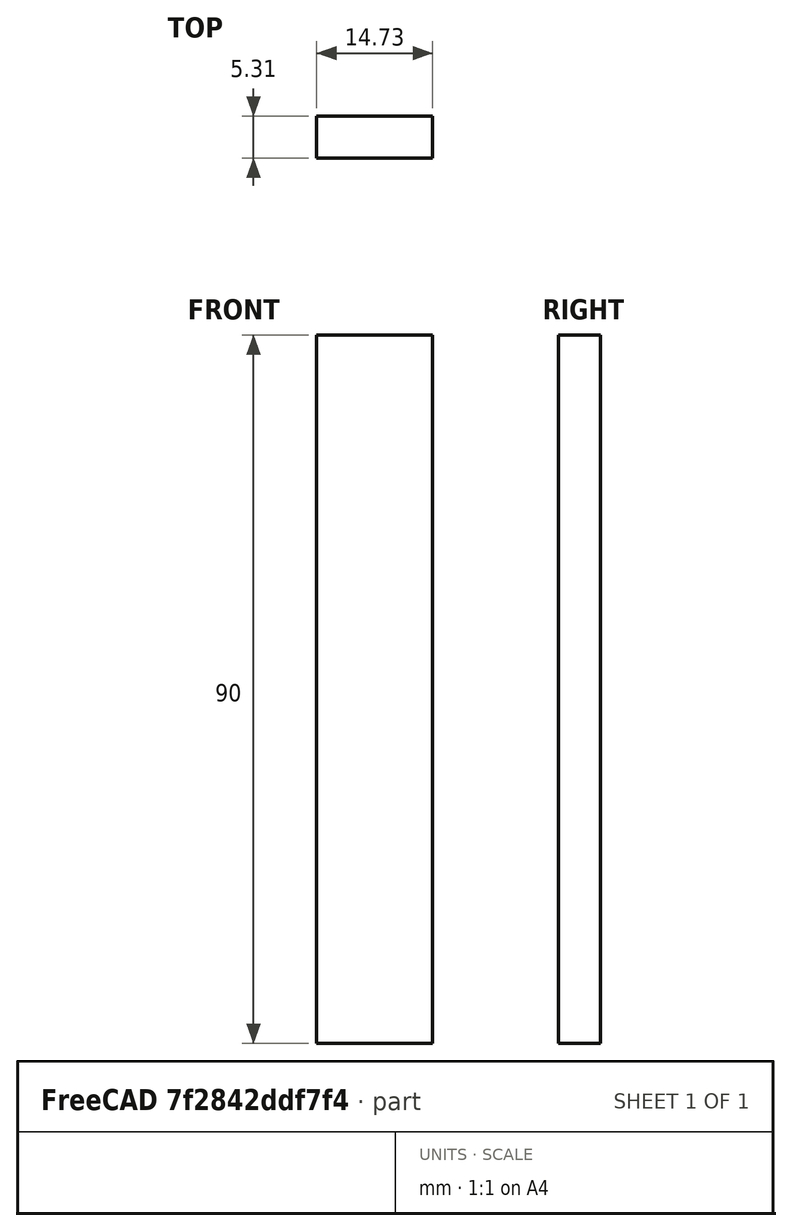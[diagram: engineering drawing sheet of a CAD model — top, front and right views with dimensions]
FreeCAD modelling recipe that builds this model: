
FCSTD DOCUMENT  (FreeCAD 0.19R24276 (Git))
Label: Temp_h90
License: All rights reserved
LicenseURL: http://en.wikipedia.org/wiki/All_rights_reserved
objects: Sketcher::SketchObject×1, PartDesign::Pad×1, PartDesign::Body×1
note: 4 computed .brp shape members not serialized (recipe doc carries the construction recipe); baked Part::Feature solids carry a one-line shape summary decoded from their .brp

FEATURE [Sketcher::SketchObject] Sketch
  FullyConstrained = false
  MapMode = 5
  Support = -> [XY_Plane]
  sketch-geometry (4):
    g0: LineSegment StartX=0 StartY=0 StartZ=0 EndX=14.7346 EndY=0 EndZ=0
    g1: LineSegment StartX=14.7346 StartY=0 StartZ=0 EndX=14.7346 EndY=5.30726 EndZ=0
    g2: LineSegment StartX=14.7346 StartY=5.30726 StartZ=0 EndX=0 EndY=5.30726 EndZ=0
    g3: LineSegment StartX=0 StartY=5.30726 StartZ=0 EndX=0 EndY=0 EndZ=0
  constraints (9):
    c: Coincident(g0,g1)
    c: Coincident(g1,g2)
    c: Coincident(g2,g3)
    c: Coincident(g3,g0)
    c: Horizontal(g0)
    c: Horizontal(g2)
    c: Vertical(g1)
    c: Vertical(g3)
    c: Coincident(g0,g-1)
FEATURE [PartDesign::Pad] Pad
  Direction = (1,1,1)
  Length = 90
  Length2 = 100
  Profile = -> Sketch
  Type = 0
FEATURE [PartDesign::Body] Body
  Group = -> [Sketch,Pad]
  Origin = -> Origin
  Tip = -> Pad
